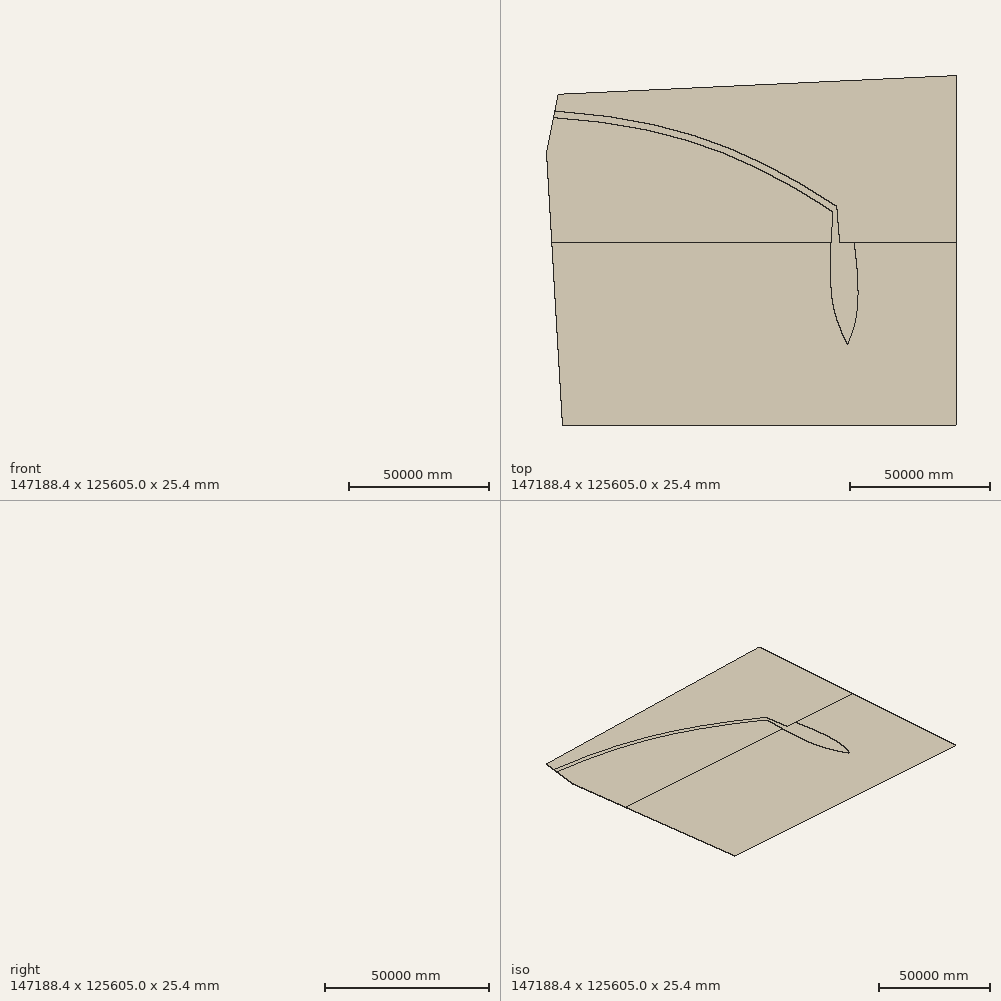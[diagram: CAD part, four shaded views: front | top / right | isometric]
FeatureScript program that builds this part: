
annotation { "Feature Type Name" : "Feature", "Feature Type Description" : "" }
export const myFeature = defineFeature(function(context is Context, id is Id, definition is map)
    precondition{}
    {
        {
            var Q0;
            Q0=qCreatedBy(makeId("Top.planeOp"),FACE);
            var sketch = newSketch(context, id + "F0", { "sketchPlane" : qUnion([Q0])});
            skLineSegment(sketch, "E0.bottom", {"start": v(-142978.65, 53034.51) * mm, "end": v(0, 59768.23) * mm});
            skLineSegment(sketch, "E0.right", {"start": v(0, 59768.23) * mm, "end": v(0, 0) * mm});
            skLineSegment(sketch, "E1.bottom", {"start": v(-145307.3, 0) * mm, "end": v(0, 0) * mm});
            skLineSegment(sketch, "E1.top", {"start": v(-141442.44, -65836.8) * mm, "end": v(0, -65836.8) * mm});
            skLineSegment(sketch, "E1.left", {"start": v(-145307.3, 0) * mm, "end": v(-141442.44, -65836.8) * mm});
            skLineSegment(sketch, "E1.right", {"start": v(0, 0) * mm, "end": v(0, -65836.8) * mm});
            skLineSegment(sketch, "E2", {"start": v(-142978.65, 53034.51) * mm, "end": v(-147188.37, 32043.32) * mm});
            skLineSegment(sketch, "E3", {"start": v(-147188.37, 32043.32) * mm, "end": v(-145307.3, 0) * mm});
            skPoint(sketch, "E4", {"position": v(-18592.8, 0) * mm});
            skPoint(sketch, "E5", {"position": v(-48768, 0) * mm});
            skPoint(sketch, "E6", {"position": v(-27792.22, 17201.79) * mm});
            skPoint(sketch, "E7", {"position": v(-44551.89, -21459.15) * mm});
            skPoint(sketch, "E8", {"position": v(-35406.45, -21482.04) * mm});
            skPoint(sketch, "E9", {"position": v(-42976.8, 0) * mm});
            skPoint(sketch, "E10", {"position": v(-42976.8, 12768.9) * mm});
            skPoint(sketch, "E11", {"position": v(-144177.32, 47057.52) * mm});
            skPoint(sketch, "E12", {"position": v(-39098.6, -37049.83) * mm});
            skFitSpline(sketch, "E13", {"points": [v(-144177.32, 47057.52) * mm, v(-42976.8, 12768.9) * mm], "startDerivative": vector(117959.45, -8151.72) * mm, "endDerivative": vector(102069.48, -67786.8) * mm});
            skFitSpline(sketch, "E14", {"points": [v(-39098.6, -37049.83) * mm, v(-42976.8, 12768.9) * mm], "startDerivative": vector(-3878.2, 49818.73) * mm, "endDerivative": vector(-3878.2, 49818.73) * mm});
            skFitSpline(sketch, "E15.0", {"points": [v(-144345.42, 44624.92) * mm, v(-141906.02, 44456.35) * mm, v(-137119, 44070.86) * mm, v(-130187.87, 43337.3) * mm, v(-123480, 42438.14) * mm, v(-116968.98, 41363.07) * mm, v(-110628.1, 40101.71) * mm, v(-104430.4, 38643.56) * mm, v(-98348.7, 36977.93) * mm, v(-92355.64, 35093.9) * mm, v(-86423.86, 32980.34) * mm, v(-80526.05, 30625.88) * mm, v(-74635.07, 28018.99) * mm, v(-68724, 25148.02) * mm, v(-62766.25, 22001.34) * mm, v(-56735.48, 18567.3) * mm, v(-50605.64, 14834.4) * mm, v(-46435.8, 12138.95) * mm, v(-44325.8, 10737.65) * mm]});
            skFitSpline(sketch, "E16.0", {"points": [v(-144009.2, 49490.12) * mm, v(-141533.63, 49319.04) * mm, v(-136669.8, 48927.44) * mm, v(-129610.3, 48180.4) * mm, v(-122761.53, 47262.48) * mm, v(-116098.29, 46162.4) * mm, v(-109595.62, 44868.97) * mm, v(-103228.84, 43371.13) * mm, v(-96973.5, 41658) * mm, v(-90805.3, 39718.94) * mm, v(-84699.95, 37543.52) * mm, v(-78633.13, 35121.53) * mm, v(-72580.34, 32442.94) * mm, v(-66516.84, 29497.81) * mm, v(-60417.59, 26276.26) * mm, v(-54257.28, 22768.32) * mm, v(-48010.31, 18963.95) * mm, v(-43770.69, 16223.3) * mm, v(-41627.8, 14800.15) * mm]});
            skFitSpline(sketch, "E17", {"points": [v(-44325.8, 10737.65) * mm, v(-44551.89, -21459.15) * mm, v(-39098.6, -37049.83) * mm], "startDerivative": vector(-4463.65, -60394.26) * mm, "endDerivative": vector(15895.06, -33616.62) * mm});
            skFitSpline(sketch, "E18", {"points": [v(-41698.37, 14847) * mm, v(-35406.45, -21482.04) * mm, v(-39098.6, -37049.83) * mm], "startDerivative": vector(22740.44, -19606.44) * mm, "endDerivative": vector(-13215.67, -35018.14) * mm});
            skLineSegment(sketch, "E19", {"start": v(-144345.42, 44624.92) * mm, "end": v(-146146.8, 44624.92) * mm});
            skLineSegment(sketch, "E20", {"start": v(-143075.28, 49424.26) * mm, "end": v(-144133.36, 49542.9) * mm});
            skSolve(sketch);
        }
        {
            var Q0;
            Q0=makeQuery(id+"F0.imprint","IMPRINT",FACE,{"disambiguationData":[TD([[makeQuery(id+"F0.imprint","IMPRINT",EDGE,{"derivedFrom":sQuery(id+"F0.wireOp",EDGE,"E0.bottom")}),-1.0]])]});
            extrude(context, id + "F1", {"entities" : qUnion([Q0]), "depth" : 25.4 * mm});
        }
        {
            var Q0;
            Q0=makeQuery(id+"F0.imprint","IMPRINT",FACE,{"disambiguationData":[TD([[makeQuery(id+"F0.imprint","IMPRINT",EDGE,{"derivedFrom":sQuery(id+"F0.wireOp",EDGE,"E1.bottom")}),-1.0]])]});
            extrude(context, id + "F2", {"entities" : qUnion([Q0]), "depth" : 25.4 * mm});
        }
        {
            var Q0;
            {var subQ7=sQuery(id+"F0.wireOp",EDGE,"E3");Q0=makeQuery(id+"F0.imprint","IMPRINT",FACE,{"disambiguationData":[TD([[makeQuery(id+"F0.imprint","IMPRINT",EDGE,{"derivedFrom":subQ7}),1.0]])]});}
            extrude(context, id + "F3", {"entities" : qUnion([Q0]), "depth" : 25.4 * mm});
        }
        {
            var Q0;
            {var subQ1=sQuery(id+"F0.wireOp",EDGE,"E1.bottom");var subQ3=sQuery(id+"F0.wireOp",EDGE,"E17");var subQ5=makeQuery(id+"F0.imprint","INTERSECT",VERTEX,{"derivedFrom":[subQ1,subQ3]});Q0=makeQuery(id+"F0.imprint","IMPRINT",FACE,{"disambiguationData":[TD([[makeQuery(id+"F0.imprint","IMPRINT",EDGE,{"disambiguationData":[TD([[subQ5,-1.0]])],"derivedFrom":subQ1}),-1.0]])]});}
            var Q1;
            {var subQ1=sQuery(id+"F0.wireOp",EDGE,"E1.bottom");var subQ3=sQuery(id+"F0.wireOp",EDGE,"E18");var subQ5=makeQuery(id+"F0.imprint","INTERSECT",VERTEX,{"derivedFrom":[subQ1,subQ3]});Q1=makeQuery(id+"F0.imprint","IMPRINT",FACE,{"disambiguationData":[TD([[makeQuery(id+"F0.imprint","IMPRINT",EDGE,{"disambiguationData":[TD([[subQ5,1.0]])],"derivedFrom":subQ1}),-1.0]])]});}
            var Q2;
            {var subQ9=sQuery(id+"F0.wireOp",EDGE,"E13");Q2=makeQuery(id+"F0.imprint","IMPRINT",FACE,{"disambiguationData":[TD([[makeQuery(id+"F0.imprint","IMPRINT",EDGE,{"derivedFrom":subQ9}),-1.0]])]});}
            extrude(context, id + "F4", {"entities" : qUnion([Q0, Q1, Q2]), "depth" : 25.4 * mm});
        }
    });
